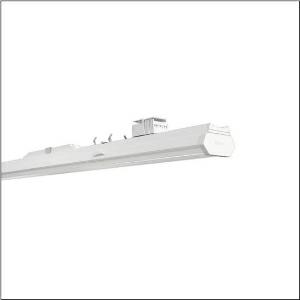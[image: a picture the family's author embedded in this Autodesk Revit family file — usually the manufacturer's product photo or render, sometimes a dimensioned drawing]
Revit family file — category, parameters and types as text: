
# Revit family: licross_r__11_protected_mo_51tp12cn49xg_4f1c
name_source: partatom
category: Lighting Fixtures
units: mm (PartAtom-declared; Revit-internal decimal feet)

## family parameters
Cut with Voids When Loaded = No
Host = Face
Light Source = No
Part Type = Normal
Room Calculation Point = No
Round Connector Dimension = Use Diameter
Shared = No

## types (1)
- --- (1 x LED, 9070 lm, 49.4 W, 4000K)
    Apparent Load = 49 VA
    CIE Flux Codes = 73 92 98 99 100
    Color Rendering = 80
    Color Temperature = 4000K
    Default Elevation = 1800 mm
    Description = Licross® 11 Protected MO, luminaire insert, of sheet steel, galvanised, coil coated, white, length: 1.500mm, width: 90mm, height: 101mm, LED rated luminous flux: 9.070lm, light colour: 840, control gear: ON/OFF Multilumen, CLOi, with plug, 3-pole, with phase selection, mains connection: 220..240V, AC, 50/60Hz, start of lifetime: 49W, end of service life: 55W, halogen-free wiring, primary light control with lens, of plastic, primary optical cover: cover, of PMMA, light emission: direct distribution, primary light characteristic: symmetric, protection rating (complete): IP64, insulation class (complete): insulation class I (protective earthing), certification: CE, ENEC, VDE, UKCA, protection symbol: D if used in an environment with conductive dust loads with corresponding accessories, impact resistance: IK06, permissible ambient temperature for indoor applications: -35..+40°C, corresponds to IFS (International Featured Standards) requirements for safety and quality in the food industry, reducing of maximum allowable ambient temperature of 5°C with ceiling mounting, LABS conformity tested according to VDMA 24364:2018-05, packaging unit: 1 piece
    Height = 92 mm
    Lamp = 1 x LED
    Lamp Light Flux = 9070 lm
    Lamp Power = 49.4 W
    Lamp count = 1
    Length = 1500 mm
    Luminous efficacy = 184 lm/W
    Manufacturer = Siteco
    ModVariant = No
    Model = 51TP12CN49XG
    Mounting Place = Ceiling
    Mounting Type = Pendant
    Number of Poles = 1
    OnlyDefault = Yes
    Power Factor = 1
    Product Name = Licross® 11 Protected MO
    Product group = luminaire insert
    ProductGroupID = 902
    Protection Class = Protection class I
    Protection Degree = IP 64
    RLX_Detail_Level = 1
    RLX_Emergency_Light_Flux = 0 lm
    RLX_Emergency_Type = 0
    RLX_Emergency_Type_DB = No
    RlxData = <blob elided: 22085 chars, md5=321458c9>
    Socket = socket
    Standby Power = 0 W
    System Light Flux = 9070 lm
    System Power = 49 W
    Type Comments = factory setting: luminous flux: 100 % | (A | C | E) | 113 mA
    Type Image = l_1256148.jpg
    URL = http://relux.com
    VarID = @adj_085872
    Voltage = 0 V
    Weight = 0.00 kg
    Width = 88 mm

## geometry (parser evidence)
native form markers: Blend x4, Sweep x12
no freeform markers — native parametric forms only
